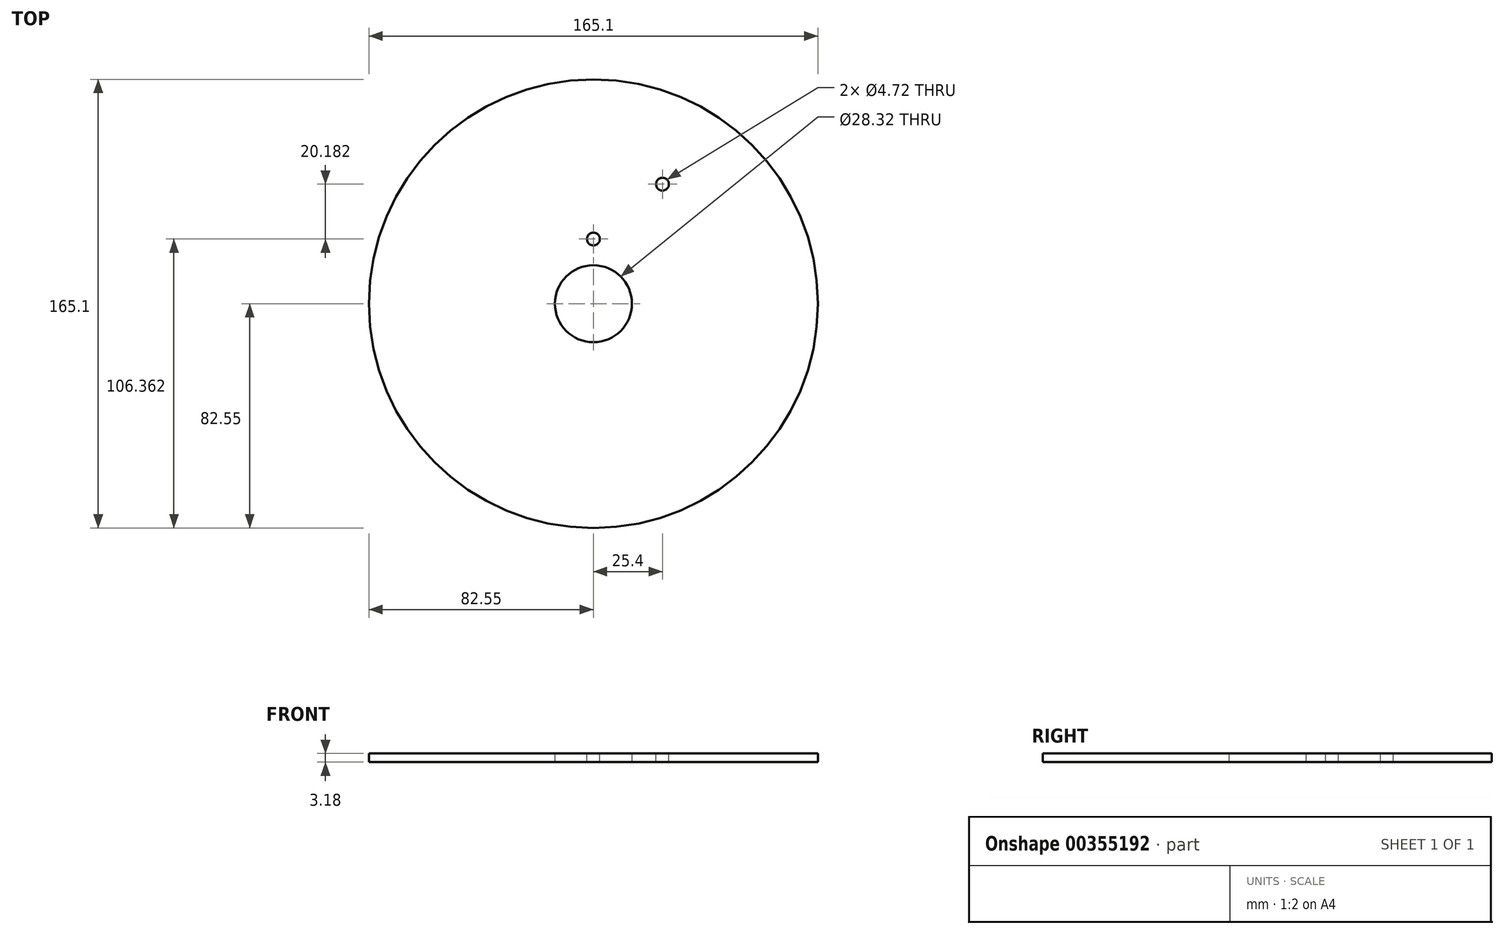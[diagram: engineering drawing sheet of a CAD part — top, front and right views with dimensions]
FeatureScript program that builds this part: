
annotation { "Feature Type Name" : "Feature", "Feature Type Description" : "" }
export const myFeature = defineFeature(function(context is Context, id is Id, definition is map)
    precondition{}
    {
        {
            var Q0;
            Q0=qCreatedBy(makeId("Top.planeOp"),FACE);
            var sketch = newSketch(context, id + "F0", { "sketchPlane" : qUnion([Q0])});
            skCircle(sketch, "E0", {"center": v(0, 0) * mm, "radius": 82.55 * mm});
            skCircle(sketch, "E1", {"center": v(0, 0) * mm, "radius": 14.16 * mm});
            skSolve(sketch);
        }
        {
            var Q0;
            Q0=makeQuery(id+"F0.imprint","IMPRINT",FACE,{"disambiguationData":[TD([[makeQuery(id+"F0.imprint","IMPRINT",EDGE,{"derivedFrom":sQuery(id+"F0.wireOp",EDGE,"E0")}),1.0]])]});
            extrude(context, id + "F1", {"entities" : qUnion([Q0]), "depth" : 3.17 * mm});
        }
        {
            var Q0;
            Q0=makeQuery(id+"F1.opExtrude","CAP_FACE",FACE,{"disambiguationData":[OSD([sQuery(id+"F0.wireOp",EDGE,"E0"),sQuery(id+"F0.wireOp",EDGE,"E1")])],"isStart":false});
            var sketch = newSketch(context, id + "F2", { "sketchPlane" : qUnion([Q0])});
            skCircle(sketch, "E2", {"center": v(0, 23.81) * mm, "radius": 2.36 * mm});
            skCircle(sketch, "E3", {"center": v(0, 76.2) * mm, "radius": 2.36 * mm, "construction": true});
            skCircle(sketch, "E4", {"center": v(25.4, 44) * mm, "radius": 2.36 * mm});
            skLineSegment(sketch, "E5", {"start": v(0, 0) * mm, "end": v(25.4, 44) * mm, "construction": true});
            skSolve(sketch);
        }
        {
            var Q0;
            Q0=qSketchRegion(id+"F2",true);
            extrude(context, id + "F3", {"entities" : qUnion([Q0]), "operationType" : NewBodyOperationType.REMOVE, "endBound" : BoundingType.THROUGH_ALL, "oppositeDirection" : true, "depth" : 25.4 * mm});
        }
    });
